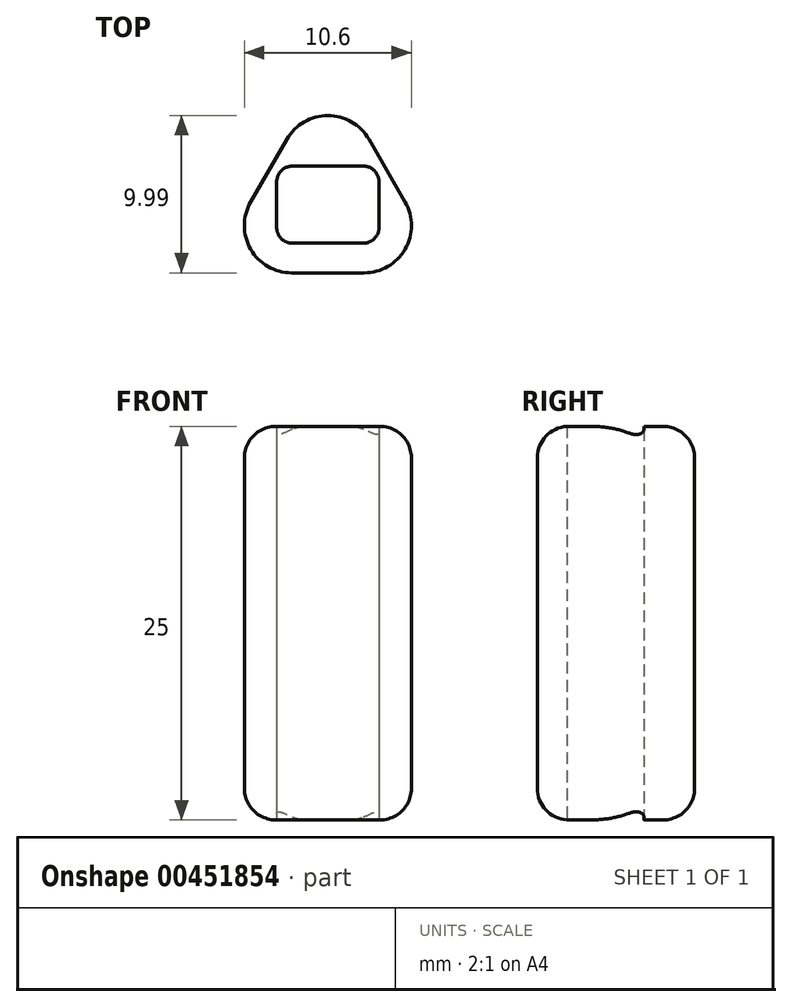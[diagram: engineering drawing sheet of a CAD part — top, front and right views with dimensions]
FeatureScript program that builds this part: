
annotation { "Feature Type Name" : "Feature", "Feature Type Description" : "" }
export const myFeature = defineFeature(function(context is Context, id is Id, definition is map)
    precondition{}
    {
        {
            var Q0;
            Q0=qCreatedBy(makeId("Top.planeOp"),FACE);
            var sketch = newSketch(context, id + "F0", { "sketchPlane" : qUnion([Q0])});
            skLineSegment(sketch, "E0.bottom", {"start": v(2.25, -2.45) * mm, "end": v(-2.25, -2.45) * mm});
            skLineSegment(sketch, "E0.top", {"start": v(2.25, 2.45) * mm, "end": v(-2.25, 2.45) * mm});
            skLineSegment(sketch, "E0.left", {"start": v(3.25, -1.45) * mm, "end": v(3.25, 1.45) * mm});
            skLineSegment(sketch, "E0.right", {"start": v(-3.25, -1.45) * mm, "end": v(-3.25, 1.45) * mm});
            skPoint(sketch, "E0.middle", {"position": v(0, 0) * mm});
            skCircle(sketch, "E1.cCircle", {"center": v(0, 0) * mm, "radius": 4.33 * mm, "construction": true});
            skLineSegment(sketch, "E1.0", {"start": v(2.3, -4.33) * mm, "end": v(-2.3, -4.33) * mm});
            skLineSegment(sketch, "E1.1", {"start": v(-4.9, 0.17) * mm, "end": v(-2.6, 4.16) * mm});
            skLineSegment(sketch, "E1.2", {"start": v(2.6, 4.16) * mm, "end": v(4.9, 0.17) * mm});
            skPoint(sketch, "E1.0.midPoint", {"position": v(0, -4.33) * mm});
            skPoint(sketch, "E2.visualSharp", {"position": v(-3.25, 2.45) * mm});
            skArc(sketch, "E2.filletArc", {"start": v(-2.25, 2.45) * mm, "mid": v(-2.96, 2.16) * mm, "end": v(-3.25, 1.45) * mm});
            skPoint(sketch, "E3.visualSharp", {"position": v(3.25, 2.45) * mm});
            skArc(sketch, "E3.filletArc", {"start": v(3.25, 1.45) * mm, "mid": v(2.96, 2.16) * mm, "end": v(2.25, 2.45) * mm});
            skPoint(sketch, "E4.visualSharp", {"position": v(3.25, -2.45) * mm});
            skArc(sketch, "E4.filletArc", {"start": v(2.25, -2.45) * mm, "mid": v(2.96, -2.16) * mm, "end": v(3.25, -1.45) * mm});
            skPoint(sketch, "E5.visualSharp", {"position": v(-3.25, -2.45) * mm});
            skArc(sketch, "E5.filletArc", {"start": v(-3.25, -1.45) * mm, "mid": v(-2.96, -2.16) * mm, "end": v(-2.25, -2.45) * mm});
            skPoint(sketch, "E6.visualSharp", {"position": v(-7.5, -4.33) * mm});
            skArc(sketch, "E6.filletArc", {"start": v(-4.9, 0.17) * mm, "mid": v(-4.9, -2.83) * mm, "end": v(-2.3, -4.33) * mm});
            skPoint(sketch, "E7.visualSharp", {"position": v(7.5, -4.33) * mm});
            skArc(sketch, "E7.filletArc", {"start": v(2.3, -4.33) * mm, "mid": v(4.9, -2.83) * mm, "end": v(4.9, 0.17) * mm});
            skPoint(sketch, "E8.visualSharp", {"position": v(0, 8.66) * mm});
            skArc(sketch, "E8.filletArc", {"start": v(2.6, 4.16) * mm, "mid": v(0, 5.66) * mm, "end": v(-2.6, 4.16) * mm});
            skSolve(sketch);
        }
        {
            var Q0;
            Q0=makeQuery(id+"F0.imprint","IMPRINT",FACE,{"disambiguationData":[TD([[makeQuery(id+"F0.imprint","IMPRINT",EDGE,{"derivedFrom":sQuery(id+"F0.wireOp",EDGE,"E0.bottom")}),1.0]])]});
            extrude(context, id + "F1", {"entities" : qUnion([Q0]), "depth" : 25 * mm, "offsetDistance" : 25 * mm});
        }
        {
            var Q0;
            Q0=makeQuery(id+"F1.opExtrude","CAP_EDGE",EDGE,{"disambiguationData":[OSD([sQuery(id+"F0.wireOp",EDGE,"E8.filletArc")])],"isStart":false});
            var Q1;
            Q1=makeQuery(id+"F1.opExtrude","CAP_EDGE",EDGE,{"disambiguationData":[OSD([sQuery(id+"F0.wireOp",EDGE,"E1.2")])],"isStart":false});
            var Q2;
            Q2=makeQuery(id+"F1.opExtrude","CAP_EDGE",EDGE,{"disambiguationData":[OSD([sQuery(id+"F0.wireOp",EDGE,"E1.1")])],"isStart":false});
            var Q3;
            Q3=makeQuery(id+"F1.opExtrude","CAP_EDGE",EDGE,{"disambiguationData":[OSD([sQuery(id+"F0.wireOp",EDGE,"E6.filletArc")])],"isStart":false});
            var Q4;
            Q4=makeQuery(id+"F1.opExtrude","CAP_EDGE",EDGE,{"disambiguationData":[OSD([sQuery(id+"F0.wireOp",EDGE,"E1.0")])],"isStart":false});
            var Q5;
            Q5=makeQuery(id+"F1.opExtrude","CAP_EDGE",EDGE,{"disambiguationData":[OSD([sQuery(id+"F0.wireOp",EDGE,"E7.filletArc")])],"isStart":false});
            var Q6;
            Q6=makeQuery(id+"F1.opExtrude","CAP_EDGE",EDGE,{"disambiguationData":[OSD([sQuery(id+"F0.wireOp",EDGE,"E7.filletArc")])],"isStart":true});
            var Q7;
            Q7=makeQuery(id+"F1.opExtrude","CAP_EDGE",EDGE,{"disambiguationData":[OSD([sQuery(id+"F0.wireOp",EDGE,"E1.2")])],"isStart":true});
            var Q8;
            Q8=makeQuery(id+"F1.opExtrude","CAP_EDGE",EDGE,{"disambiguationData":[OSD([sQuery(id+"F0.wireOp",EDGE,"E8.filletArc")])],"isStart":true});
            var Q9;
            Q9=makeQuery(id+"F1.opExtrude","CAP_EDGE",EDGE,{"disambiguationData":[OSD([sQuery(id+"F0.wireOp",EDGE,"E1.1")])],"isStart":true});
            var Q10;
            Q10=makeQuery(id+"F1.opExtrude","CAP_EDGE",EDGE,{"disambiguationData":[OSD([sQuery(id+"F0.wireOp",EDGE,"E6.filletArc")])],"isStart":true});
            var Q11;
            Q11=makeQuery(id+"F1.opExtrude","CAP_EDGE",EDGE,{"disambiguationData":[OSD([sQuery(id+"F0.wireOp",EDGE,"E1.0")])],"isStart":true});
            fillet(context, id + "F2", {"entities" : qUnion([Q0, Q1, Q2, Q3, Q4, Q5, Q6, Q7, Q8, Q9, Q10, Q11]), "radius" : 2 * mm, "tangentPropagation" : true, "allowEdgeOverflow" : false});
        }
    });
